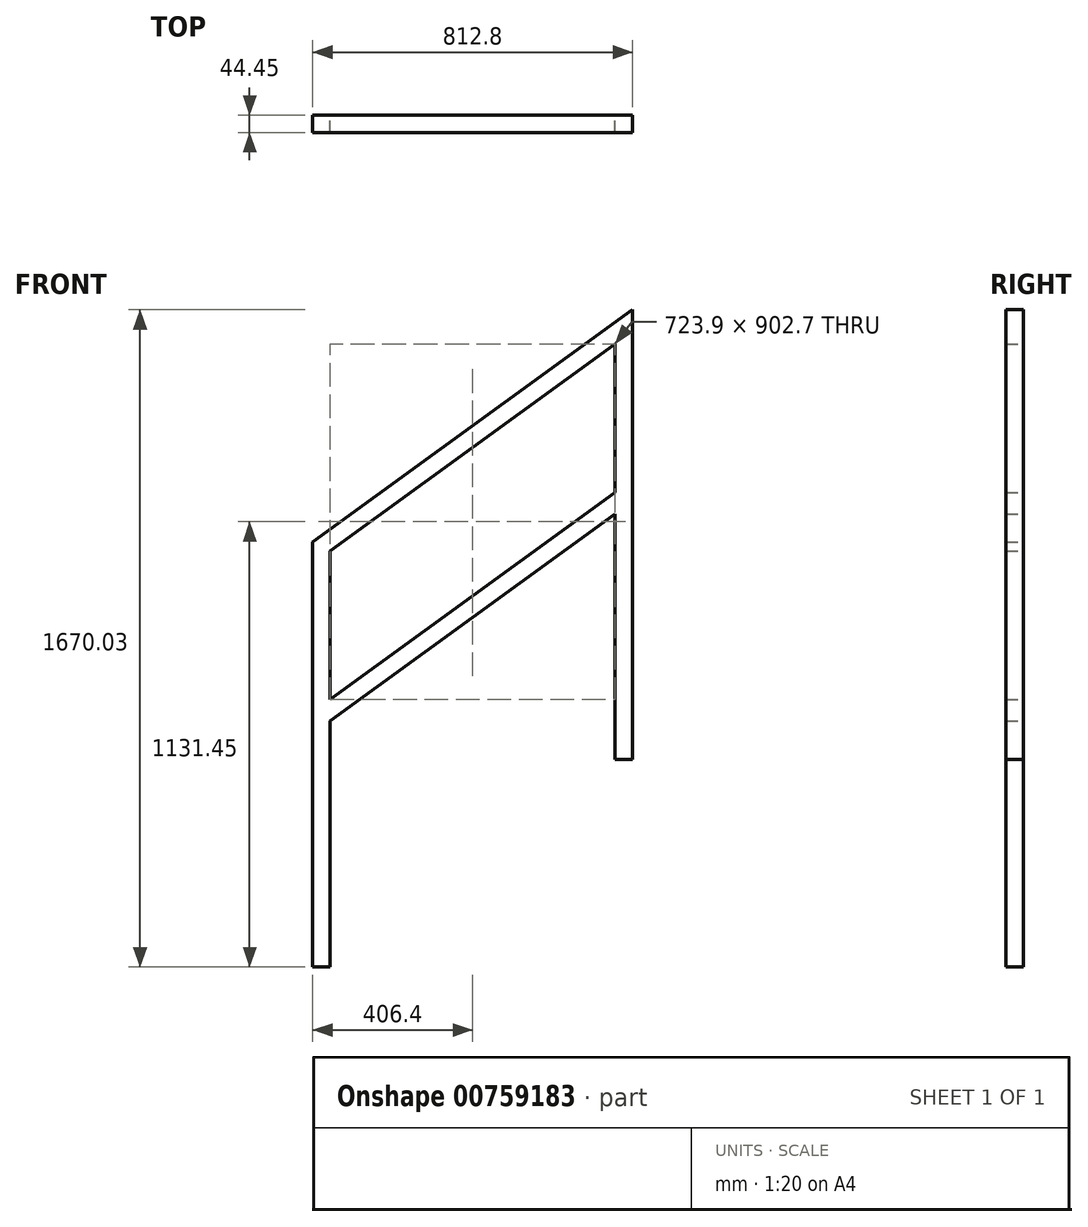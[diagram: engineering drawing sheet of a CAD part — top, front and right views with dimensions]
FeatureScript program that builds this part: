
annotation { "Feature Type Name" : "Feature", "Feature Type Description" : "" }
export const myFeature = defineFeature(function(context is Context, id is Id, definition is map)
    precondition{}
    {
        {
            var Q0;
            Q0=qCreatedBy(makeId("Front.planeOp"),FACE);
            var sketch = newSketch(context, id + "F0", { "sketchPlane" : qUnion([Q0])});
            skLineSegment(sketch, "E0", {"start": v(0, 0) * mm, "end": v(812.8, 590.53) * mm});
            skLineSegment(sketch, "E1", {"start": v(812.8, -552.47) * mm, "end": v(812.8, 590.53) * mm});
            skPoint(sketch, "E2.first.point", {"position": v(812.8, 590.53) * mm});
            skPoint(sketch, "E2.second.point", {"position": v(812.8, 590.53) * mm});
            skLineSegment(sketch, "E3", {"start": v(768.35, 503.3) * mm, "end": v(44.45, -22.65) * mm});
            skLineSegment(sketch, "E4", {"start": v(768.35, -552.47) * mm, "end": v(768.35, 503.3) * mm});
            skLineSegment(sketch, "E5", {"start": v(0, 0) * mm, "end": v(0, -1079.5) * mm});
            skLineSegment(sketch, "E6", {"start": v(44.45, -22.65) * mm, "end": v(44.45, -1079.5) * mm});
            skLineSegment(sketch, "E7", {"start": v(0, -1079.5) * mm, "end": v(44.45, -1079.5) * mm});
            skLineSegment(sketch, "E8", {"start": v(44.45, -399.4) * mm, "end": v(768.35, 126.54) * mm});
            skLineSegment(sketch, "E9", {"start": v(44.45, -454.35) * mm, "end": v(768.35, 71.6) * mm});
            skLineSegment(sketch, "E10", {"start": v(768.35, -552.47) * mm, "end": v(812.8, -552.47) * mm});
            skSolve(sketch);
        }
        {
            var Q0;
            {var subQ0=sQuery(id+"F0.wireOp",EDGE,"E8");Q0=makeQuery(id+"F0.imprint","IMPRINT",FACE,{"disambiguationData":[TD([[makeQuery(id+"F0.imprint","IMPRINT",EDGE,{"derivedFrom":subQ0}),-1.0]])]});}
            var Q1;
            Q1=makeQuery(id+"F0.imprint","IMPRINT",FACE,{"disambiguationData":[TD([[makeQuery(id+"F0.imprint","IMPRINT",EDGE,{"derivedFrom":sQuery(id+"F0.wireOp",EDGE,"E1")}),1.0]])]});
            extrude(context, id + "F1", {"entities" : qUnion([Q0, Q1]), "depth" : 44.45 * mm, "offsetDistance" : 25.4 * mm});
        }
    });
